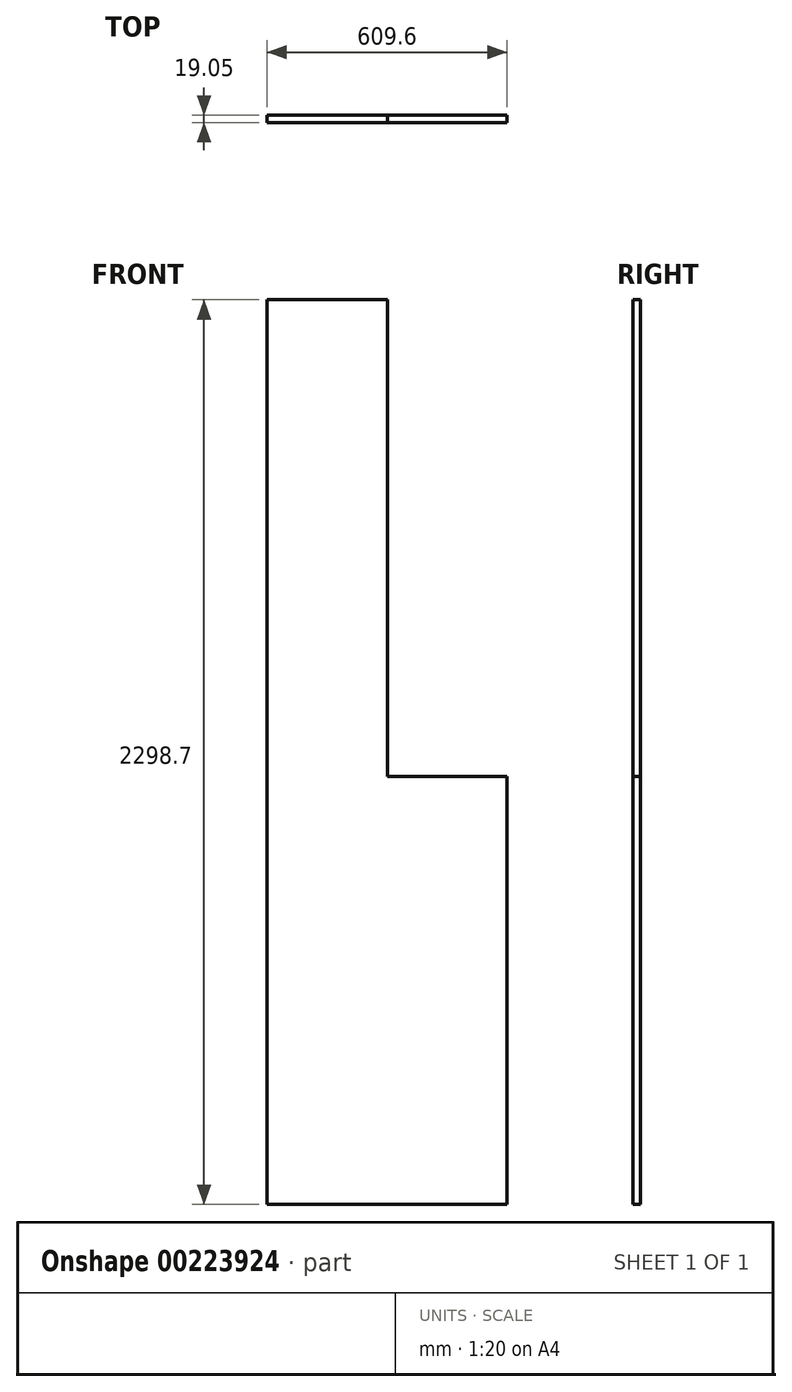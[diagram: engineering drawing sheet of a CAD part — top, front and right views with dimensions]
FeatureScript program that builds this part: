
annotation { "Feature Type Name" : "Feature", "Feature Type Description" : "" }
export const myFeature = defineFeature(function(context is Context, id is Id, definition is map)
    precondition{}
    {
        {
            var Q0;
            Q0=qCreatedBy(makeId("Front.planeOp"),FACE);
            var sketch = newSketch(context, id + "F0", { "sketchPlane" : qUnion([Q0])});
            skLineSegment(sketch, "E0.bottom", {"start": v(0, 0) * mm, "end": v(609.6, 0) * mm});
            skLineSegment(sketch, "E0.top", {"start": v(0, 2298.7) * mm, "end": v(609.6, 2298.7) * mm});
            skLineSegment(sketch, "E0.left", {"start": v(0, 0) * mm, "end": v(0, 2298.7) * mm});
            skLineSegment(sketch, "E0.right", {"start": v(609.6, 0) * mm, "end": v(609.6, 2298.7) * mm});
            skSolve(sketch);
        }
        {
            var Q0;
            Q0=makeQuery(id+"F0.imprint","IMPRINT",FACE,{"disambiguationData":[TD([[makeQuery(id+"F0.imprint","IMPRINT",EDGE,{"derivedFrom":sQuery(id+"F0.wireOp",EDGE,"E0.bottom")}),1.0]])]});
            extrude(context, id + "F1", {"entities" : qUnion([Q0]), "oppositeDirection" : true, "depth" : 19.05 * mm});
        }
        {
            var Q0;
            Q0=qCreatedBy(makeId("Front.planeOp"),FACE);
            var sketch = newSketch(context, id + "F2", { "sketchPlane" : qUnion([Q0])});
            skLineSegment(sketch, "E1.bottom", {"start": v(610.24, 2306.1) * mm, "end": v(305.44, 2306.1) * mm});
            skLineSegment(sketch, "E1.top", {"start": v(610.24, 1086.9) * mm, "end": v(305.44, 1086.9) * mm});
            skLineSegment(sketch, "E1.left", {"start": v(610.24, 2306.1) * mm, "end": v(610.24, 1086.9) * mm});
            skLineSegment(sketch, "E1.right", {"start": v(305.44, 2306.1) * mm, "end": v(305.44, 1086.9) * mm});
            skSolve(sketch);
        }
        {
            var Q0;
            Q0=makeQuery(id+"F2.imprint","IMPRINT",FACE,{"disambiguationData":[TD([[makeQuery(id+"F2.imprint","IMPRINT",EDGE,{"derivedFrom":sQuery(id+"F2.wireOp",EDGE,"E1.bottom")}),1.0]])]});
            extrude(context, id + "F3", {"entities" : qUnion([Q0]), "operationType" : NewBodyOperationType.REMOVE, "endBound" : BoundingType.THROUGH_ALL, "oppositeDirection" : true, "depth" : 25.4 * mm});
        }
    });
